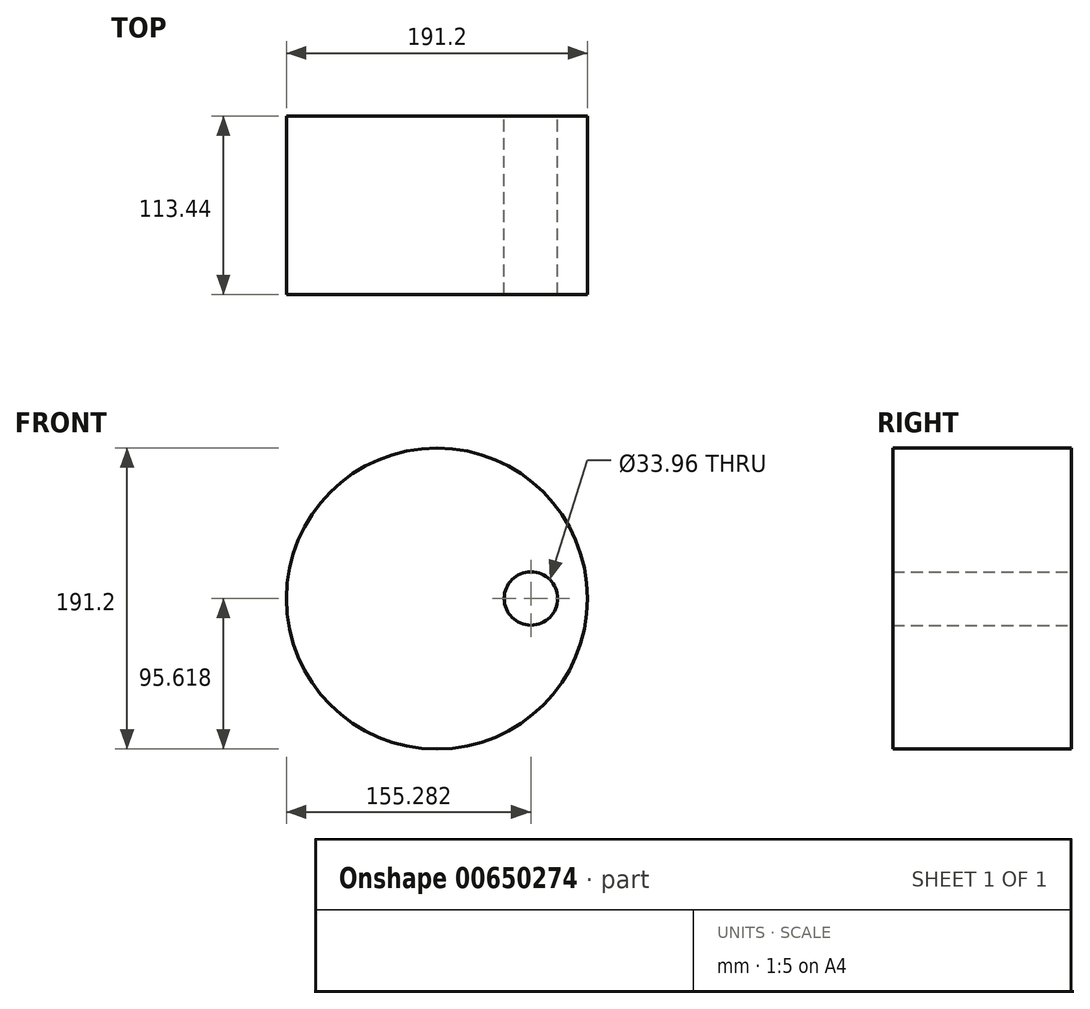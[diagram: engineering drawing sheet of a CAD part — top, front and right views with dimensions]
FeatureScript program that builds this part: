
annotation { "Feature Type Name" : "Feature", "Feature Type Description" : "" }
export const myFeature = defineFeature(function(context is Context, id is Id, definition is map)
    precondition{}
    {
        {
            var Q0;
            Q0=qCreatedBy(makeId("Front.planeOp"),FACE);
            var sketch = newSketch(context, id + "F0", { "sketchPlane" : qUnion([Q0])});
            skCircle(sketch, "E0", {"center": v(0, 28.52) * mm, "radius": 95.6 * mm});
            skCircle(sketch, "E1", {"center": v(59.68, 28.54) * mm, "radius": 16.98 * mm});
            skSolve(sketch);
        }
        {
            var Q0;
            Q0 = qSketchRegion(id + "F0", true);
            extrude(context, id + "F1", {"entities" : qUnion([Q0]), "depth" : 113.44 * mm, "offsetDistance" : 25.4 * mm});
        }
    });
